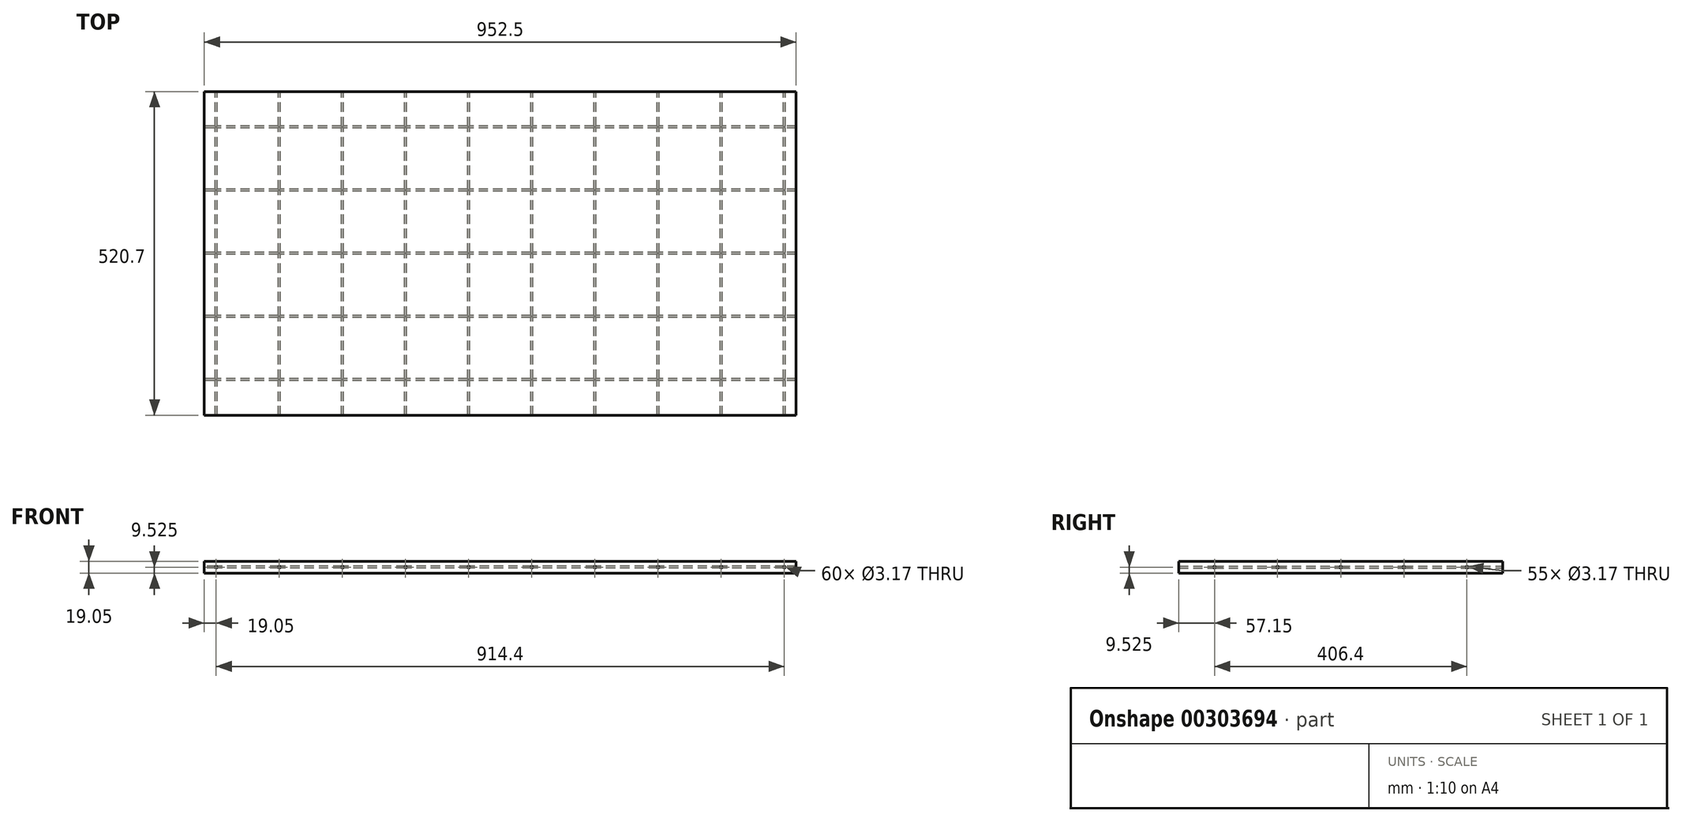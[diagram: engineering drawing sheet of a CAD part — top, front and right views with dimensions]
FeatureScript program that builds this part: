
annotation { "Feature Type Name" : "Feature", "Feature Type Description" : "" }
export const myFeature = defineFeature(function(context is Context, id is Id, definition is map)
    precondition{}
    {
        {
            var Q0;
            Q0=qCreatedBy(makeId("Top.planeOp"),FACE);
            var sketch = newSketch(context, id + "F0", { "sketchPlane" : qUnion([Q0])});
            skLineSegment(sketch, "E0.bottom", {"start": v(0, 0) * mm, "end": v(952.5, 0) * mm});
            skLineSegment(sketch, "E0.top", {"start": v(0, -520.7) * mm, "end": v(952.5, -520.7) * mm});
            skLineSegment(sketch, "E0.left", {"start": v(0, 0) * mm, "end": v(0, -520.7) * mm});
            skLineSegment(sketch, "E0.right", {"start": v(952.5, 0) * mm, "end": v(952.5, -520.7) * mm});
            skSolve(sketch);
        }
        {
            var Q0;
            Q0 = qSketchRegion(id + "F0", true);
            extrude(context, id + "F1", {"entities" : qUnion([Q0]), "oppositeDirection" : true, "depth" : 19.05 * mm});
        }
        {
            var Q0;
            Q0=qCreatedBy(makeId("Right.planeOp"),FACE);
            var sketch = newSketch(context, id + "F2", { "sketchPlane" : qUnion([Q0])});
            skCircle(sketch, "E1", {"center": v(-463.55, -9.53) * mm, "radius": 1.59 * mm});
            skCircle(sketch, "E2.1.0.0", {"center": v(-361.95, -9.53) * mm, "radius": 1.59 * mm});
            skCircle(sketch, "E2.2.0.0", {"center": v(-260.35, -9.53) * mm, "radius": 1.59 * mm});
            skCircle(sketch, "E2.3.0.0", {"center": v(-158.75, -9.53) * mm, "radius": 1.59 * mm});
            skCircle(sketch, "E2.4.0.0", {"center": v(-57.15, -9.53) * mm, "radius": 1.59 * mm});
            skLineSegment(sketch, "E2.direction1", {"start": v(-463.55, -9.53) * mm, "end": v(-361.95, -9.53) * mm, "construction": true});
            skSolve(sketch);
        }
        {
            var Q0;
            Q0 = qSketchRegion(id + "F2", true);
            extrude(context, id + "F3", {"entities" : qUnion([Q0]), "operationType" : NewBodyOperationType.REMOVE, "endBound" : BoundingType.THROUGH_ALL, "depth" : 25.4 * mm});
        }
        {
            var Q0;
            Q0=qCreatedBy(makeId("Front.planeOp"),FACE);
            var sketch = newSketch(context, id + "F4", { "sketchPlane" : qUnion([Q0])});
            skCircle(sketch, "E3", {"center": v(19.05, -9.53) * mm, "radius": 1.59 * mm});
            skCircle(sketch, "E4.1.0.0", {"center": v(120.65, -9.53) * mm, "radius": 1.59 * mm});
            skCircle(sketch, "E4.2.0.0", {"center": v(222.25, -9.53) * mm, "radius": 1.59 * mm});
            skCircle(sketch, "E4.3.0.0", {"center": v(323.85, -9.53) * mm, "radius": 1.59 * mm});
            skCircle(sketch, "E4.4.0.0", {"center": v(425.45, -9.53) * mm, "radius": 1.59 * mm});
            skCircle(sketch, "E4.5.0.0", {"center": v(527.05, -9.53) * mm, "radius": 1.59 * mm});
            skCircle(sketch, "E4.6.0.0", {"center": v(628.65, -9.53) * mm, "radius": 1.59 * mm});
            skCircle(sketch, "E4.7.0.0", {"center": v(730.25, -9.53) * mm, "radius": 1.59 * mm});
            skCircle(sketch, "E4.8.0.0", {"center": v(831.85, -9.53) * mm, "radius": 1.59 * mm});
            skCircle(sketch, "E4.9.0.0", {"center": v(933.45, -9.53) * mm, "radius": 1.59 * mm});
            skLineSegment(sketch, "E4.direction1", {"start": v(19.05, -9.53) * mm, "end": v(120.65, -9.53) * mm, "construction": true});
            skSolve(sketch);
        }
        {
            var Q0;
            Q0 = qSketchRegion(id + "F4", true);
            extrude(context, id + "F5", {"entities" : qUnion([Q0]), "operationType" : NewBodyOperationType.REMOVE, "endBound" : BoundingType.THROUGH_ALL, "depth" : 25.4 * mm});
        }
    });
